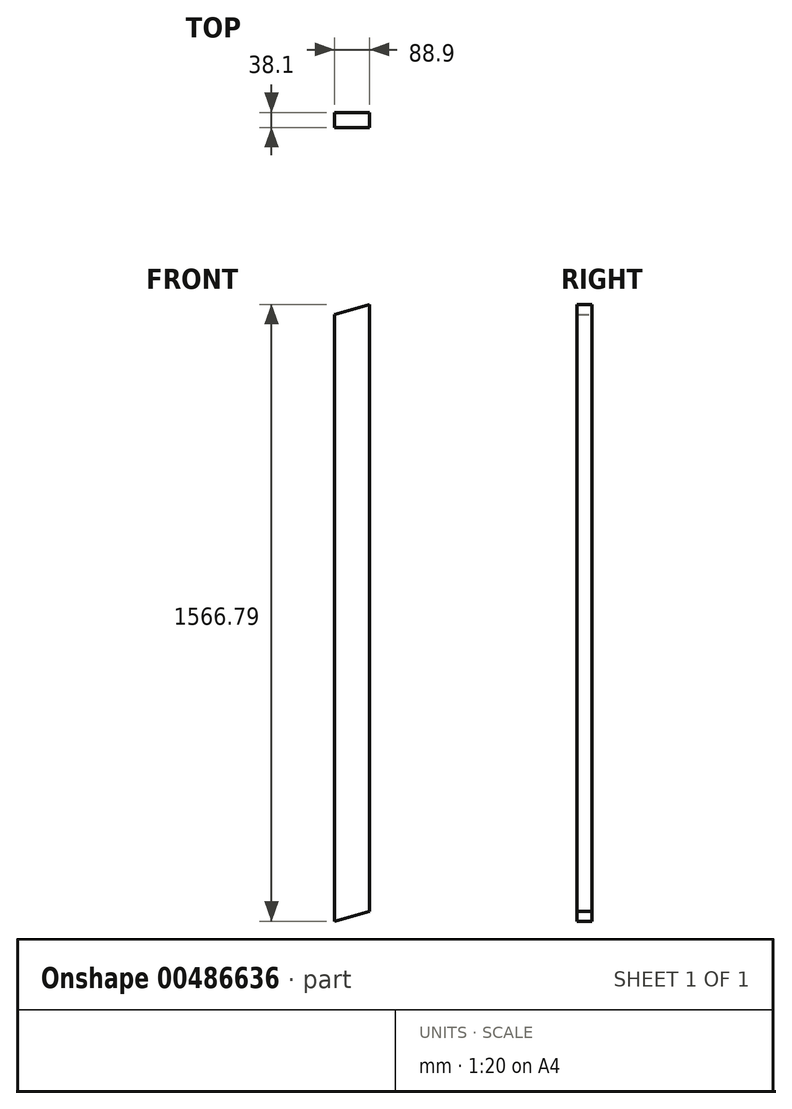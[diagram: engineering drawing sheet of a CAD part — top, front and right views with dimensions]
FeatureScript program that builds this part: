
annotation { "Feature Type Name" : "Feature", "Feature Type Description" : "" }
export const myFeature = defineFeature(function(context is Context, id is Id, definition is map)
    precondition{}
    {
        {
            var Q0;
            Q0=qCreatedBy(makeId("Front.planeOp"),FACE);
            var sketch = newSketch(context, id + "F0", { "sketchPlane" : qUnion([Q0])});
            skLineSegment(sketch, "E0.left", {"start": v(0, 0) * mm, "end": v(0, 1516) * mm});
            skLineSegment(sketch, "E0.right", {"start": v(88.9, 0) * mm, "end": v(88.9, 1541.4) * mm});
            skLineSegment(sketch, "E1", {"start": v(0, 1516) * mm, "end": v(88.9, 1541.4) * mm});
            skLineSegment(sketch, "E2", {"start": v(0, 0) * mm, "end": v(0, -25.4) * mm});
            skLineSegment(sketch, "E3", {"start": v(0, -25.4) * mm, "end": v(88.9, 0) * mm});
            skSolve(sketch);
        }
        {
            var Q0;
            Q0=makeQuery(id+"F0.imprint","IMPRINT",FACE,{"disambiguationData":[TD([[makeQuery(id+"F0.imprint","IMPRINT",EDGE,{"derivedFrom":sQuery(id+"F0.wireOp",EDGE,"E0.left")}),-1.0]])]});
            extrude(context, id + "F1", {"entities" : qUnion([Q0]), "depth" : 38.1 * mm});
        }
    });
